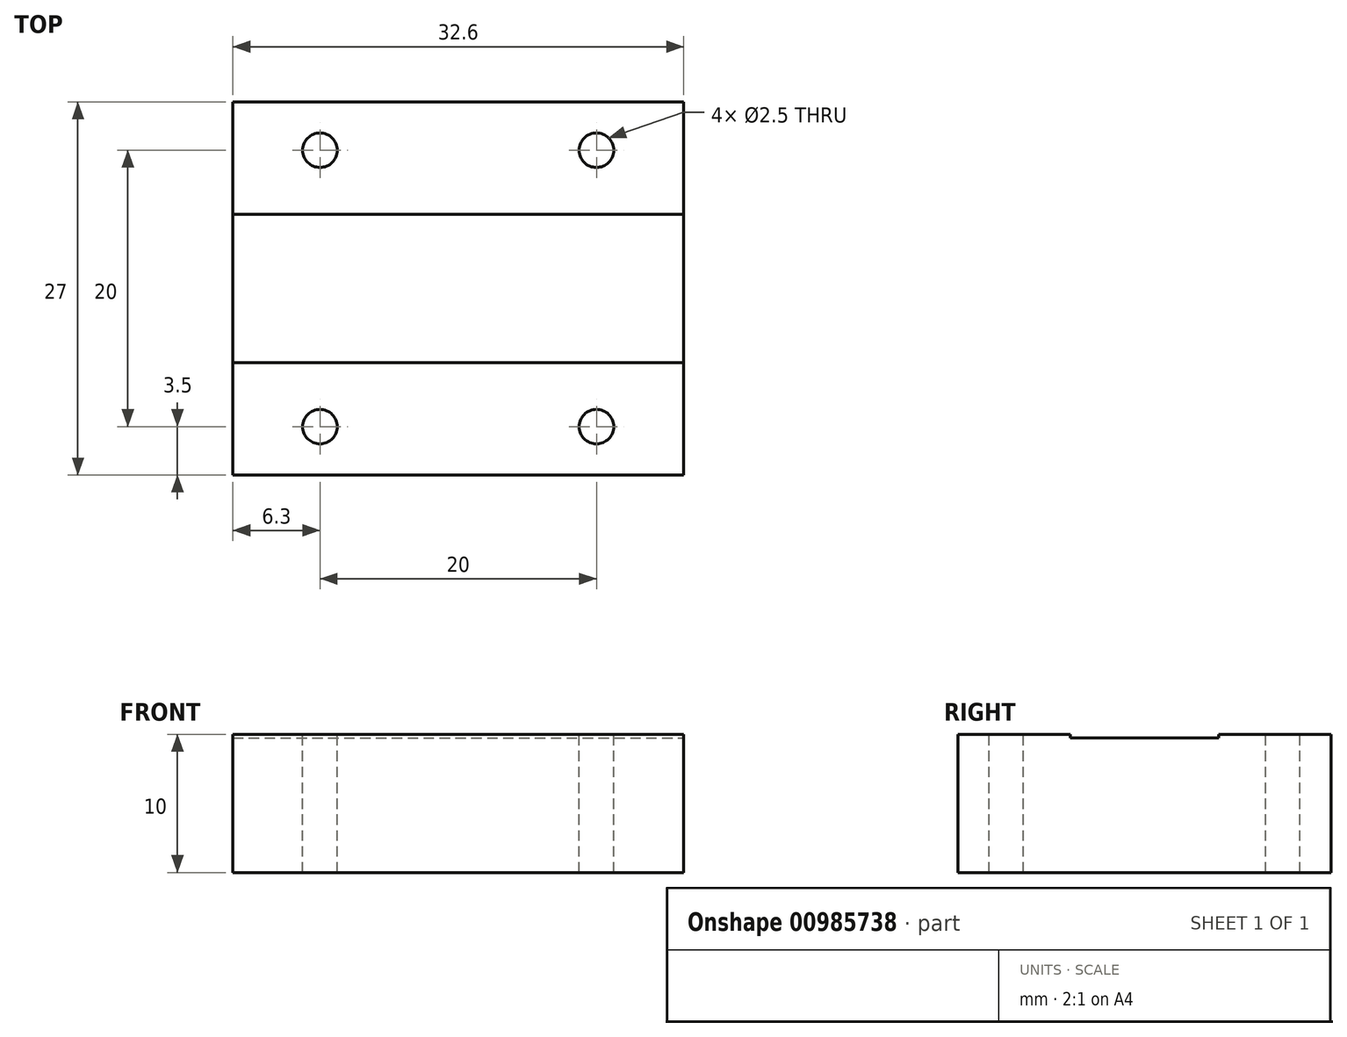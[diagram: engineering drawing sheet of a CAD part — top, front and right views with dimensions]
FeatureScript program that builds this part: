
annotation { "Feature Type Name" : "Feature", "Feature Type Description" : "" }
export const myFeature = defineFeature(function(context is Context, id is Id, definition is map)
    precondition{}
    {
        {
            var Q0;
            Q0=qCreatedBy(makeId("Top.planeOp"),FACE);
            var sketch = newSketch(context, id + "F0", { "sketchPlane" : qUnion([Q0])});
            skLineSegment(sketch, "E0.bottom", {"start": v(0, 0) * mm, "end": v(32.6, 0) * mm});
            skLineSegment(sketch, "E0.top", {"start": v(0, 27) * mm, "end": v(32.6, 27) * mm});
            skLineSegment(sketch, "E0.left", {"start": v(0, 0) * mm, "end": v(0, 27) * mm});
            skLineSegment(sketch, "E0.right", {"start": v(32.6, 0) * mm, "end": v(32.6, 27) * mm});
            skSolve(sketch);
        }
        {
            var Q0;
            Q0 = qSketchRegion(id + "F0", true);
            extrude(context, id + "F1", {"entities" : qUnion([Q0]), "depth" : 10 * mm, "offsetDistance" : 25.4 * mm});
        }
        {
            var Q0;
            Q0=makeQuery(id+"F1.opExtrude","CAP_FACE",FACE,{"disambiguationData":[OSD([sQuery(id+"F0.wireOp",EDGE,"E0.bottom"),sQuery(id+"F0.wireOp",EDGE,"E0.top"),sQuery(id+"F0.wireOp",EDGE,"E0.left"),sQuery(id+"F0.wireOp",EDGE,"E0.right")])],"isStart":false});
            var sketch = newSketch(context, id + "F2", { "sketchPlane" : qUnion([Q0])});
            skLineSegment(sketch, "E1.bottom", {"start": v(0, 18.88) * mm, "end": v(32.6, 18.88) * mm});
            skLineSegment(sketch, "E1.top", {"start": v(0, 8.12) * mm, "end": v(32.6, 8.12) * mm});
            skLineSegment(sketch, "E1.left", {"start": v(0, 18.88) * mm, "end": v(0, 8.12) * mm});
            skLineSegment(sketch, "E1.right", {"start": v(32.6, 18.88) * mm, "end": v(32.6, 8.12) * mm});
            skPoint(sketch, "E2", {"position": v(0, 13.5) * mm});
            skSolve(sketch);
        }
        {
            var Q0;
            Q0 = qSketchRegion(id + "F2", true);
            extrude(context, id + "F3", {"entities" : qUnion([Q0]), "operationType" : NewBodyOperationType.REMOVE, "oppositeDirection" : true, "depth" : .25 * mm, "offsetDistance" : 25.4 * mm});
        }
        {
            var Q0;
            {var subQ0=sQuery(id+"F0.wireOp",EDGE,"E0.top");var subQ1=sQuery(id+"F0.wireOp",EDGE,"E0.left");var subQ2=sQuery(id+"F0.wireOp",EDGE,"E0.right");Q0=makeQuery(id+"F3.boolean.opBoolean","SPLIT",FACE,{"disambiguationData":[TD([makeQuery(id+"F1.opExtrude","SWEPT_FACE",FACE,{"disambiguationData":[OSD([subQ0])]})])],"derivedFrom":makeQuery(id+"F1.opExtrude","CAP_FACE",FACE,{"disambiguationData":[OSD([sQuery(id+"F0.wireOp",EDGE,"E0.bottom"),subQ0,subQ1,subQ2])],"isStart":false})});}
            var sketch = newSketch(context, id + "F4", { "sketchPlane" : qUnion([Q0])});
            skLineSegment(sketch, "E3.bottom", {"start": v(6.3, 23.5) * mm, "end": v(26.3, 23.5) * mm});
            skLineSegment(sketch, "E3.top", {"start": v(6.3, 3.5) * mm, "end": v(26.3, 3.5) * mm});
            skLineSegment(sketch, "E3.left", {"start": v(6.3, 23.5) * mm, "end": v(6.3, 3.5) * mm});
            skLineSegment(sketch, "E3.right", {"start": v(26.3, 23.5) * mm, "end": v(26.3, 3.5) * mm});
            skLineSegment(sketch, "E4", {"start": v(26.3, 13.5) * mm, "end": v(32.6, 13.5) * mm});
            skLineSegment(sketch, "E5", {"start": v(16.3, 23.5) * mm, "end": v(16.3, 27) * mm});
            skPoint(sketch, "E6", {"position": v(6.3, 23.5) * mm});
            skPoint(sketch, "E7", {"position": v(26.3, 23.5) * mm});
            skPoint(sketch, "E8", {"position": v(26.3, 3.5) * mm});
            skPoint(sketch, "E9", {"position": v(6.3, 3.5) * mm});
            skSolve(sketch);
        }
        {
            var Q0;
            Q0=sQuery(id+"F4.wireOp",VERTEX,"E6");
            var Q1;
            Q1=sQuery(id+"F4.wireOp",VERTEX,"E7");
            var Q2;
            Q2=sQuery(id+"F4.wireOp",VERTEX,"E8");
            var Q3;
            Q3=sQuery(id+"F4.wireOp",VERTEX,"E9");
            var Q4;
            Q4=makeQuery(id+"F1.opExtrude","SWEPT_BODY",BODY,{"disambiguationData":[OSD([sQuery(id+"F0.wireOp",EDGE,"E0.bottom"),sQuery(id+"F0.wireOp",EDGE,"E0.top"),sQuery(id+"F0.wireOp",EDGE,"E0.left"),sQuery(id+"F0.wireOp",EDGE,"E0.right")])]});
            hole(context, id + "F5", {"style" : HoleStyle.SIMPLE, "endStyle" : HoleEndStyle.BLIND, "standardTappedOrClearance" : lookupTablePath({ "standard" : "ISO", "engagement" : "75%", "pitch" : "0.5 mm", "size" : "M3", "type" : "Tapped" }), "standardBlindInLast" : lookupTablePath({ "standard" : "ISO", "fit" : "Normal", "engagement" : "75%", "pitch" : "0.5 mm", "size" : "M3", "type" : "Clearance & tapped" }), "holeDiameter" : 2.5 * mm, "majorDiameter" : 3 * mm, "showTappedDepth" : true, "holeDepth" : 14.2 * mm, "isTappedThrough" : true, "tappedDepth" : 12.7 * mm, "tapClearance" : 3, "startFromSketch" : true, "locations" : qUnion([Q0, Q1, Q2, Q3]), "scope" : qUnion([Q4])});
        }
    });
